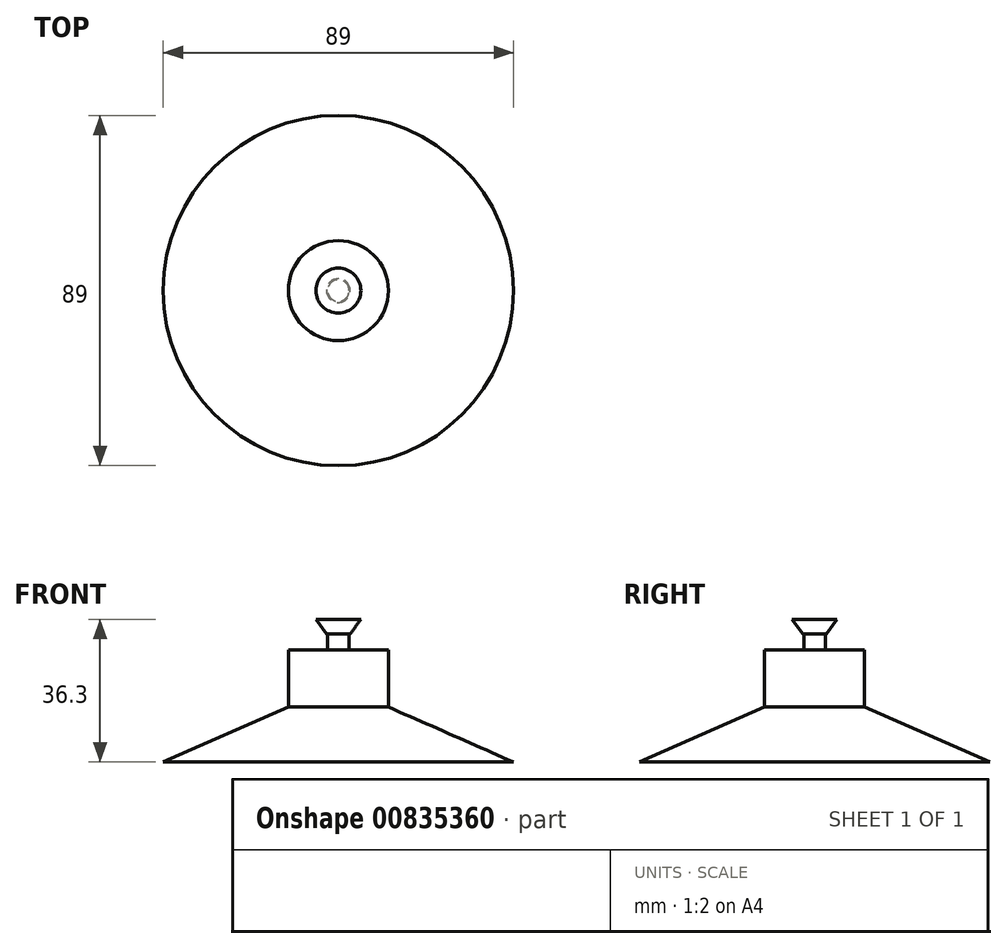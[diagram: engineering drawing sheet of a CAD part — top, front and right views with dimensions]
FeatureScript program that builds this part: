
annotation { "Feature Type Name" : "Feature", "Feature Type Description" : "" }
export const myFeature = defineFeature(function(context is Context, id is Id, definition is map)
    precondition{}
    {
        {
            var Q0;
            Q0=qCreatedBy(makeId("Top.planeOp"),FACE);
            var sketch = newSketch(context, id + "F0", { "sketchPlane" : qUnion([Q0])});
            skCircle(sketch, "E0", {"center": v(0, 0) * mm, "radius": 12.7 * mm});
            skSolve(sketch);
        }
        {
            var Q0;
            Q0 = qSketchRegion(id + "F0", true);
            extrude(context, id + "F1", {"entities" : qUnion([Q0]), "depth" : 14.5 * mm, "offsetDistance" : 25 * mm});
        }
        {
            var Q0;
            Q0=qCreatedBy(makeId("Front.planeOp"),FACE);
            var sketch = newSketch(context, id + "F2", { "sketchPlane" : qUnion([Q0])});
            skLineSegment(sketch, "E1", {"start": v(-12.7, 0) * mm, "end": v(-44.5, -14) * mm});
            skLineSegment(sketch, "E2", {"start": v(-12.7, 0) * mm, "end": v(0, 0) * mm});
            skLineSegment(sketch, "E3", {"start": v(0, 0) * mm, "end": v(0, -14) * mm});
            skLineSegment(sketch, "E4", {"start": v(0, -14) * mm, "end": v(-44.5, -14) * mm});
            skSolve(sketch);
        }
        {
            var Q0;
            Q0 = qSketchRegion(id + "F2", true);
            var Q1;
            Q1=sQuery(id+"F2.wireOp",EDGE,"E3");
            revolve(context, id + "F3", {"operationType" : NewBodyOperationType.ADD, "surfaceOperationType" : NewSurfaceOperationType.NEW, "entities" : qUnion([Q0]), "axis" : qUnion([Q1]), "revolveType" : RevolveType.FULL});
        }
        {
            var Q0;
            Q0=makeQuery(id+"F1.opExtrude","CAP_FACE",FACE,{"disambiguationData":[OSD([sQuery(id+"F0.wireOp",EDGE,"E0")])],"isStart":false});
            var sketch = newSketch(context, id + "F4", { "sketchPlane" : qUnion([Q0])});
            skCircle(sketch, "E5", {"center": v(0, 0) * mm, "radius": 2.75 * mm});
            skSolve(sketch);
        }
        {
            var Q0;
            Q0 = qSketchRegion(id + "F4", true);
            extrude(context, id + "F5", {"entities" : qUnion([Q0]), "operationType" : NewBodyOperationType.ADD, "depth" : 4 * mm, "offsetDistance" : 25 * mm});
        }
        {
            var Q0;
            Q0=qCreatedBy(makeId("Right.planeOp"),FACE);
            var sketch = newSketch(context, id + "F6", { "sketchPlane" : qUnion([Q0])});
            skLineSegment(sketch, "E6", {"start": v(0, 18.5) * mm, "end": v(3, 18.5) * mm});
            skLineSegment(sketch, "E7", {"start": v(3, 18.5) * mm, "end": v(5.7, 22.3) * mm});
            skLineSegment(sketch, "E8", {"start": v(5.7, 22.3) * mm, "end": v(0, 22.3) * mm});
            skLineSegment(sketch, "E9", {"start": v(0, 22.3) * mm, "end": v(0, 18.5) * mm});
            skSolve(sketch);
        }
        {
            var Q0;
            Q0 = qSketchRegion(id + "F6", true);
            var Q1;
            Q1=sQuery(id+"F6.wireOp",EDGE,"E9");
            revolve(context, id + "F7", {"surfaceOperationType" : NewSurfaceOperationType.NEW, "entities" : qUnion([Q0]), "axis" : qUnion([Q1]), "revolveType" : RevolveType.FULL});
        }
    });
